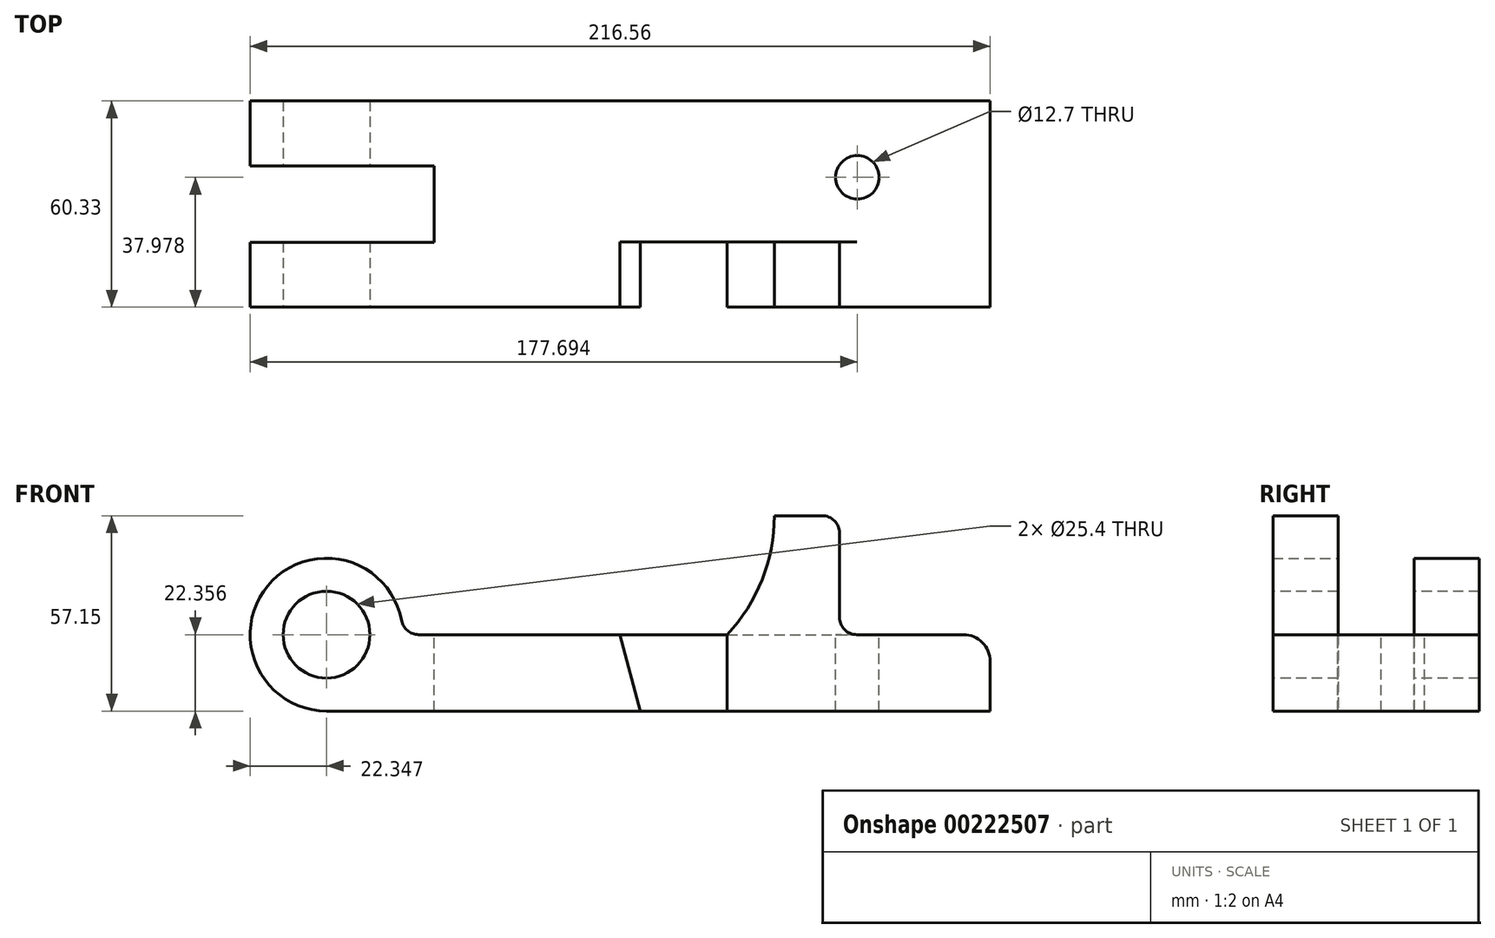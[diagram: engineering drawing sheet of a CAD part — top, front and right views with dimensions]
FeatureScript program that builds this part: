
annotation { "Feature Type Name" : "Feature", "Feature Type Description" : "" }
export const myFeature = defineFeature(function(context is Context, id is Id, definition is map)
    precondition{}
    {
        {
            var Q0;
            Q0=qCreatedBy(makeId("Front.planeOp"),FACE);
            var sketch = newSketch(context, id + "F0", { "sketchPlane" : qUnion([Q0])});
            skArc(sketch, "E0", {"start": v(-73.66, 16.93) * mm, "mid": v(-112.83, 27.06) * mm, "end": v(-95.62, -9.56) * mm});
            skLineSegment(sketch, "E1", {"start": v(-95.62, -9.56) * mm, "end": v(98.59, -9.56) * mm});
            skLineSegment(sketch, "E2", {"start": v(98.59, -9.56) * mm, "end": v(98.59, 4.92) * mm});
            skLineSegment(sketch, "E3", {"start": v(90.71, 12.8) * mm, "end": v(59.55, 12.8) * mm});
            skLineSegment(sketch, "E4", {"start": v(54.47, 17.88) * mm, "end": v(54.47, 42.51) * mm});
            skLineSegment(sketch, "E5", {"start": v(49.39, 47.6) * mm, "end": v(35.42, 47.6) * mm});
            skLineSegment(sketch, "E6", {"start": v(21.62, 12.8) * mm, "end": v(-68.67, 12.8) * mm});
            skPoint(sketch, "E7.visualSharp", {"position": v(54.47, 12.8) * mm});
            skArc(sketch, "E7.filletArc", {"start": v(54.47, 17.88) * mm, "mid": v(55.95, 14.28) * mm, "end": v(59.55, 12.8) * mm});
            skPoint(sketch, "E8.visualSharp", {"position": v(98.59, 12.8) * mm});
            skArc(sketch, "E8.filletArc", {"start": v(98.59, 4.92) * mm, "mid": v(96.28, 10.49) * mm, "end": v(90.71, 12.8) * mm});
            skLineSegment(sketch, "E9", {"start": v(21.62, -15.96) * mm, "end": v(21.62, 12.8) * mm, "construction": true});
            skArc(sketch, "E10", {"start": v(21.62, 12.8) * mm, "mid": v(31.84, 28.88) * mm, "end": v(35.42, 47.6) * mm});
            skPoint(sketch, "E11.visualSharp", {"position": v(54.47, 47.6) * mm});
            skArc(sketch, "E11.filletArc", {"start": v(54.47, 42.51) * mm, "mid": v(52.98, 46.1) * mm, "end": v(49.39, 47.6) * mm});
            skPoint(sketch, "E12.visualSharp", {"position": v(-73.27, 12.8) * mm});
            skArc(sketch, "E12.filletArc", {"start": v(-73.66, 16.93) * mm, "mid": v(-71.9, 13.97) * mm, "end": v(-68.67, 12.8) * mm});
            skSolve(sketch);
        }
        {
            var Q0;
            Q0 = qSketchRegion(id + "F0", true);
            extrude(context, id + "F1", {"entities" : qUnion([Q0]), "depth" : 60.32 * mm});
        }
        {
            var Q0;
            Q0=makeQuery(id+"F1.opExtrude","CAP_FACE",FACE,{"disambiguationData":[OSD([sQuery(id+"F0.wireOp",EDGE,"E0"),sQuery(id+"F0.wireOp",EDGE,"E1"),sQuery(id+"F0.wireOp",EDGE,"E2"),sQuery(id+"F0.wireOp",EDGE,"E3"),sQuery(id+"F0.wireOp",EDGE,"E4"),sQuery(id+"F0.wireOp",EDGE,"E5"),sQuery(id+"F0.wireOp",EDGE,"E6"),sQuery(id+"F0.wireOp",EDGE,"E7.filletArc"),sQuery(id+"F0.wireOp",EDGE,"E8.filletArc"),sQuery(id+"F0.wireOp",EDGE,"E10"),sQuery(id+"F0.wireOp",EDGE,"E11.filletArc"),sQuery(id+"F0.wireOp",EDGE,"E12.filletArc")])],"isStart":false});
            var sketch = newSketch(context, id + "F2", { "sketchPlane" : qUnion([Q0])});
            skCircle(sketch, "E13", {"center": v(-95.62, 12.8) * mm, "radius": 12.7 * mm});
            skLineSegment(sketch, "E14", {"start": v(-9.77, 12.8) * mm, "end": v(-3.78, -9.56) * mm});
            skLineSegment(sketch, "E15", {"start": v(-3.78, -9.56) * mm, "end": v(21.62, -9.56) * mm});
            skLineSegment(sketch, "E16", {"start": v(21.62, -9.56) * mm, "end": v(21.62, 12.8) * mm});
            skLineSegment(sketch, "E17", {"start": v(21.62, 12.8) * mm, "end": v(-9.77, 12.8) * mm});
            skArc(sketch, "E18.0", {"start": v(-73.66, 16.93) * mm, "mid": v(-112.83, 27.06) * mm, "end": v(-95.62, -9.56) * mm});
            skSolve(sketch);
        }
        {
            var Q0;
            Q0=makeQuery(id+"F2.imprint","IMPRINT",FACE,{"disambiguationData":[TD([[makeQuery(id+"F2.imprint","IMPRINT",EDGE,{"derivedFrom":sQuery(id+"F2.wireOp",EDGE,"E13")}),1.0]])]});
            extrude(context, id + "F3", {"entities" : qUnion([Q0]), "operationType" : NewBodyOperationType.REMOVE, "endBound" : BoundingType.THROUGH_ALL, "oppositeDirection" : true, "depth" : 25.4 * mm});
        }
        {
            var Q0;
            Q0=makeQuery(id+"F2.imprint","IMPRINT",FACE,{"disambiguationData":[TD([[makeQuery(id+"F2.imprint","IMPRINT",EDGE,{"derivedFrom":sQuery(id+"F2.wireOp",EDGE,"E14")}),1.0]])]});
            extrude(context, id + "F4", {"entities" : qUnion([Q0]), "operationType" : NewBodyOperationType.REMOVE, "oppositeDirection" : true, "depth" : 19.05 * mm});
        }
        {
            var Q0;
            Q0=makeQuery(id+"F1.opExtrude","SWEPT_FACE",FACE,{"disambiguationData":[OSD([sQuery(id+"F0.wireOp",EDGE,"E5")])]});
            var sketch = newSketch(context, id + "F5", { "sketchPlane" : qUnion([Q0])});
            skLineSegment(sketch, "E19.0.0", {"start": v(-9.77, -41.28) * mm, "end": v(21.62, -41.28) * mm, "construction": true});
            skLineSegment(sketch, "E19.0.1", {"start": v(21.62, -41.28) * mm, "end": v(21.62, 0) * mm, "construction": true});
            skLineSegment(sketch, "E19.0.2", {"start": v(21.62, 0) * mm, "end": v(-68.67, 0) * mm, "construction": true});
            skLineSegment(sketch, "E19.0.3", {"start": v(-68.67, 0) * mm, "end": v(-68.67, -60.33) * mm, "construction": true});
            skLineSegment(sketch, "E19.0.4", {"start": v(-68.67, -60.33) * mm, "end": v(-9.77, -60.33) * mm, "construction": true});
            skLineSegment(sketch, "E19.0.5", {"start": v(-9.77, -60.32) * mm, "end": v(-9.77, -41.28) * mm, "construction": true});
            skLineSegment(sketch, "E20.0.0", {"start": v(59.55, 0) * mm, "end": v(54.47, 0) * mm, "construction": true});
            skLineSegment(sketch, "E20.0.1", {"start": v(54.47, 0) * mm, "end": v(54.47, -60.33) * mm, "construction": true});
            skLineSegment(sketch, "E20.0.2", {"start": v(54.47, -60.33) * mm, "end": v(59.55, -60.33) * mm, "construction": true});
            skLineSegment(sketch, "E20.0.3", {"start": v(59.55, -60.33) * mm, "end": v(59.55, 0) * mm, "construction": true});
            skLineSegment(sketch, "E21.bottom", {"start": v(21.62, -41.28) * mm, "end": v(59.55, -41.28) * mm});
            skLineSegment(sketch, "E21.top", {"start": v(21.62, 0) * mm, "end": v(59.55, 0) * mm});
            skLineSegment(sketch, "E21.left", {"start": v(21.62, -41.28) * mm, "end": v(21.62, 0) * mm});
            skLineSegment(sketch, "E21.right", {"start": v(59.55, -41.28) * mm, "end": v(59.55, 0) * mm});
            skSolve(sketch);
        }
        {
            var Q0;
            Q0 = qSketchRegion(id + "F5", true);
            extrude(context, id + "F6", {"entities" : qUnion([Q0]), "operationType" : NewBodyOperationType.REMOVE, "oppositeDirection" : true, "depth" : 34.8 * mm});
        }
        {
            var Q0;
            Q0=qCreatedBy(makeId("Top.planeOp"),FACE);
            var sketch = newSketch(context, id + "F7", { "sketchPlane" : qUnion([Q0])});
            skCircle(sketch, "E22", {"center": v(59.72, -22.35) * mm, "radius": 6.35 * mm});
            skLineSegment(sketch, "E23.0.0", {"start": v(-73.66, 0) * mm, "end": v(-117.97, 0) * mm, "construction": true});
            skLineSegment(sketch, "E23.0.1", {"start": v(-95.62, 0) * mm, "end": v(-95.62, -60.33) * mm, "construction": true});
            skLineSegment(sketch, "E23.0.2", {"start": v(-117.97, -60.33) * mm, "end": v(-73.66, -60.33) * mm, "construction": true});
            skLineSegment(sketch, "E23.0.3", {"start": v(-73.66, -60.33) * mm, "end": v(-73.66, 0) * mm, "construction": true});
            skLineSegment(sketch, "E24", {"start": v(-117.97, 0) * mm, "end": v(-117.97, -60.33) * mm});
            skLineSegment(sketch, "E25.bottom", {"start": v(-117.97, -19) * mm, "end": v(-64.19, -19) * mm});
            skLineSegment(sketch, "E25.top", {"start": v(-117.97, -41.33) * mm, "end": v(-64.19, -41.33) * mm});
            skLineSegment(sketch, "E25.left", {"start": v(-117.97, -19) * mm, "end": v(-117.97, -41.33) * mm});
            skLineSegment(sketch, "E25.right", {"start": v(-64.19, -19) * mm, "end": v(-64.19, -41.33) * mm});
            skSolve(sketch);
        }
        {
            var Q0;
            Q0 = qSketchRegion(id + "F7", true);
            extrude(context, id + "F8", {"entities" : qUnion([Q0]), "operationType" : NewBodyOperationType.REMOVE, "endBound" : BoundingType.THROUGH_ALL, "oppositeDirection" : true, "depth" : 25.4 * mm, "hasSecondDirection" : true, "secondDirectionBound" : SecondDirectionBoundingType.THROUGH_ALL, "secondDirectionOppositeDirection" : false, "secondDirectionDepth" : 25.4 * mm});
        }
    });
